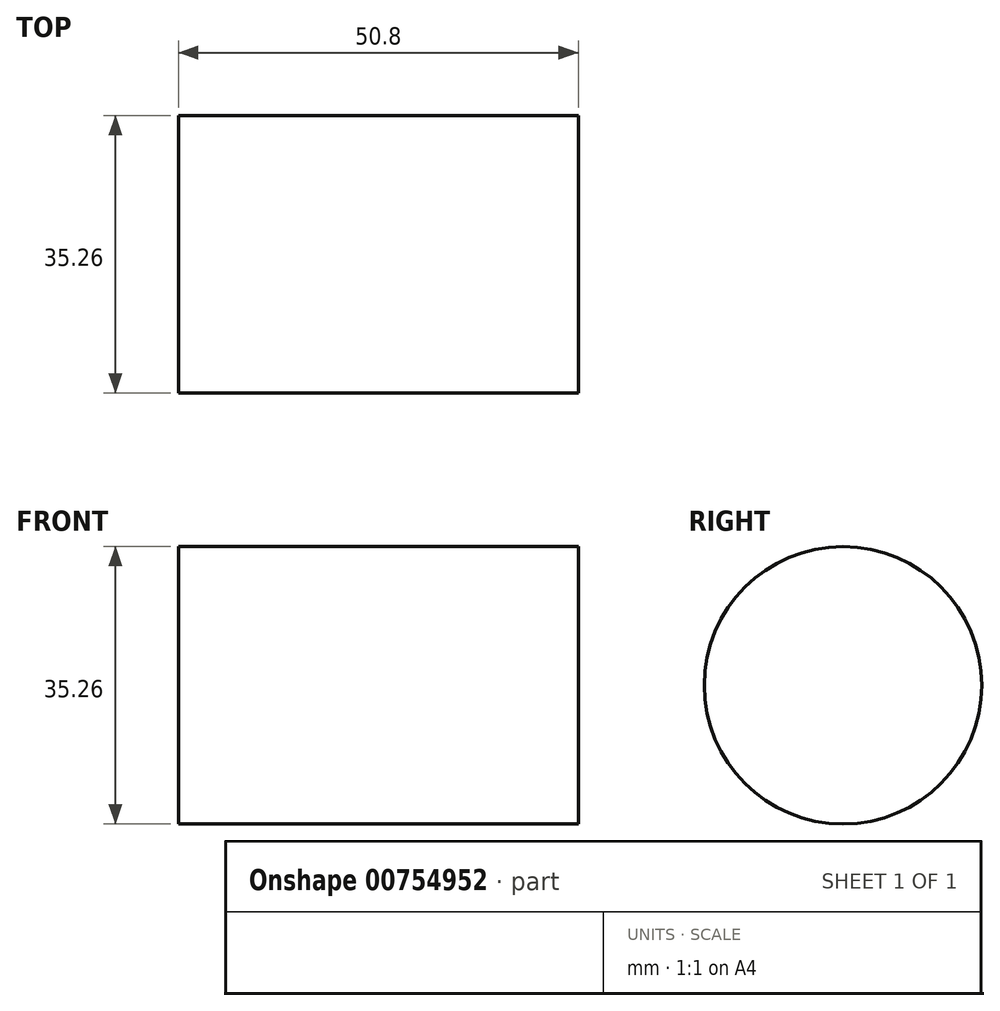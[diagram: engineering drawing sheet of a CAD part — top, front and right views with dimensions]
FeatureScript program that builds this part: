
annotation { "Feature Type Name" : "Feature", "Feature Type Description" : "" }
export const myFeature = defineFeature(function(context is Context, id is Id, definition is map)
    precondition{}
    {
        {
            var Q0;
            Q0=qCreatedBy(makeId("Right.planeOp"),FACE);
            var sketch = newSketch(context, id + "F0", { "sketchPlane" : qUnion([Q0])});
            skCircle(sketch, "E0", {"center": v(0, 0) * mm, "radius": 17.63 * mm});
            skSolve(sketch);
        }
        {
            var Q0;
            Q0=sQuery(id+"F0.wireOp",EDGE,"E0");
            extrude(context, id + "F1", {"bodyType" : ToolBodyType.SURFACE, "surfaceEntities" : qUnion([Q0]), "depth" : 50.8 * mm, "offsetDistance" : 25.4 * mm});
        }
    });
